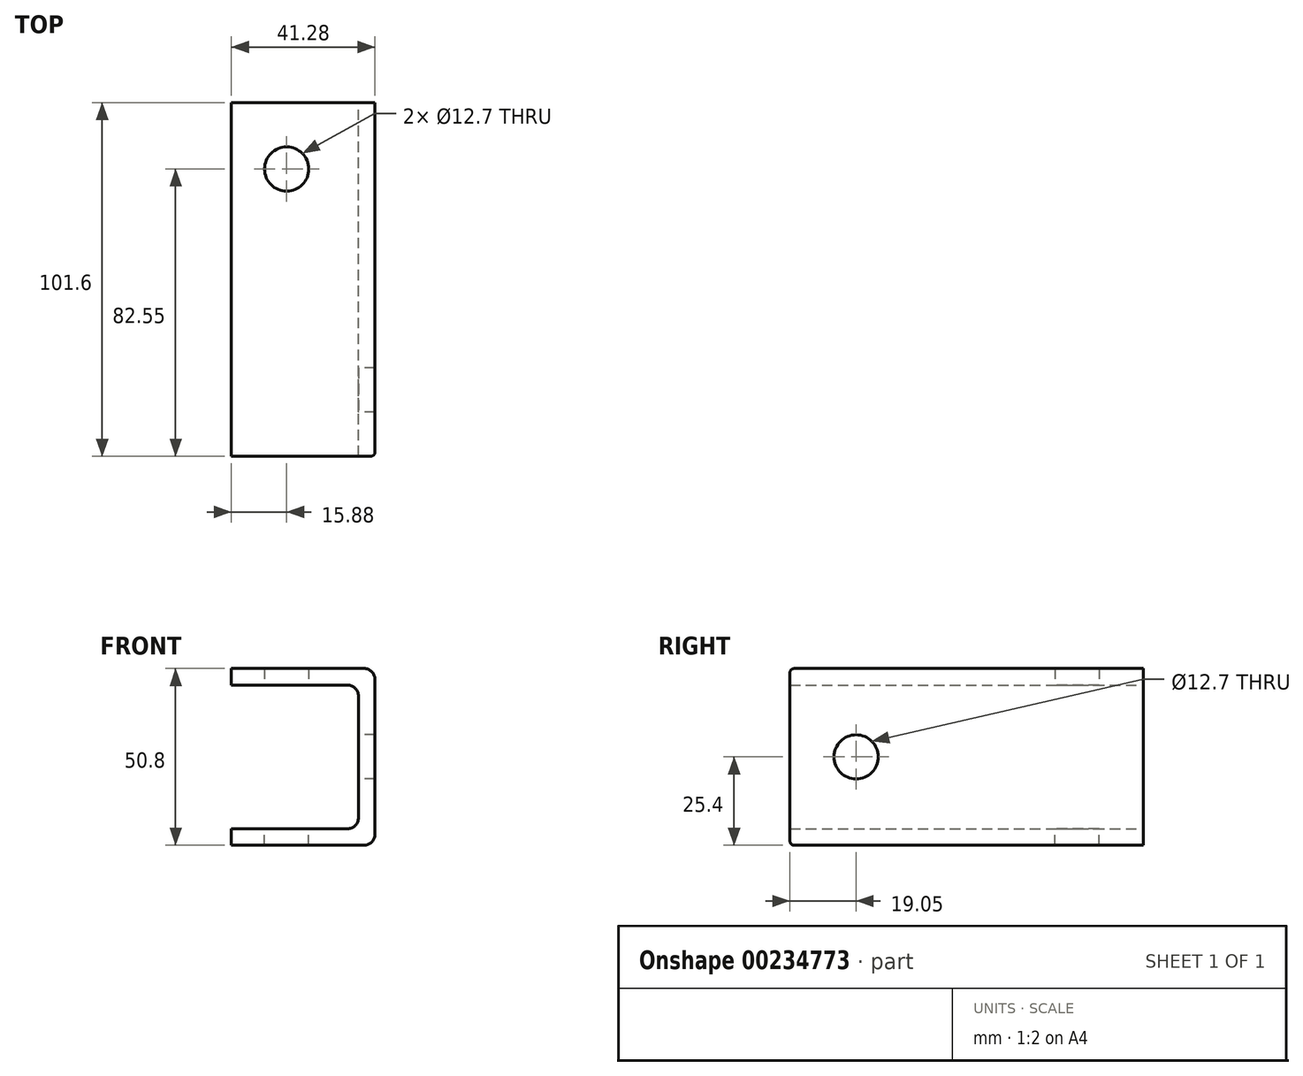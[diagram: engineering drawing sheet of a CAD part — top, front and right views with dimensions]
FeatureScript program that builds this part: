
annotation { "Feature Type Name" : "Feature", "Feature Type Description" : "" }
export const myFeature = defineFeature(function(context is Context, id is Id, definition is map)
    precondition{}
    {
        {
            var Q0;
            Q0=qCreatedBy(makeId("Front.planeOp"),FACE);
            var sketch = newSketch(context, id + "F0", { "sketchPlane" : qUnion([Q0])});
            skLineSegment(sketch, "E0.bottom", {"start": v(22.23, -25.4) * mm, "end": v(-22.23, -25.4) * mm});
            skLineSegment(sketch, "E0.top", {"start": v(22.23, 25.4) * mm, "end": v(-22.23, 25.4) * mm});
            skLineSegment(sketch, "E0.left", {"start": v(25.4, -22.23) * mm, "end": v(25.4, 22.23) * mm});
            skLineSegment(sketch, "E0.right", {"start": v(-25.4, -22.23) * mm, "end": v(-25.4, 22.23) * mm});
            skPoint(sketch, "E0.middle", {"position": v(0, 0) * mm});
            skLineSegment(sketch, "E1.bottom", {"start": v(17.46, -20.64) * mm, "end": v(-17.46, -20.64) * mm});
            skLineSegment(sketch, "E1.top", {"start": v(17.46, 20.64) * mm, "end": v(-17.46, 20.64) * mm});
            skLineSegment(sketch, "E1.left", {"start": v(20.64, -17.46) * mm, "end": v(20.64, 17.46) * mm});
            skLineSegment(sketch, "E1.right", {"start": v(-20.64, -17.46) * mm, "end": v(-20.64, 17.46) * mm});
            skPoint(sketch, "E2.visualSharp", {"position": v(-25.4, 25.4) * mm});
            skArc(sketch, "E2.filletArc", {"start": v(-22.23, 25.4) * mm, "mid": v(-24.47, 24.47) * mm, "end": v(-25.4, 22.23) * mm});
            skPoint(sketch, "E3.visualSharp", {"position": v(25.4, 25.4) * mm});
            skArc(sketch, "E3.filletArc", {"start": v(25.4, 22.23) * mm, "mid": v(24.47, 24.47) * mm, "end": v(22.23, 25.4) * mm});
            skPoint(sketch, "E4.visualSharp", {"position": v(20.64, 20.64) * mm});
            skArc(sketch, "E4.filletArc", {"start": v(20.64, 17.46) * mm, "mid": v(19.7, 19.7) * mm, "end": v(17.46, 20.64) * mm});
            skPoint(sketch, "E5.visualSharp", {"position": v(-20.64, 20.64) * mm});
            skArc(sketch, "E5.filletArc", {"start": v(-17.46, 20.64) * mm, "mid": v(-19.7, 19.7) * mm, "end": v(-20.64, 17.46) * mm});
            skPoint(sketch, "E6.visualSharp", {"position": v(-20.64, -20.64) * mm});
            skArc(sketch, "E6.filletArc", {"start": v(-20.64, -17.46) * mm, "mid": v(-19.7, -19.7) * mm, "end": v(-17.46, -20.64) * mm});
            skPoint(sketch, "E7.visualSharp", {"position": v(-25.4, -25.4) * mm});
            skArc(sketch, "E7.filletArc", {"start": v(-25.4, -22.23) * mm, "mid": v(-24.47, -24.47) * mm, "end": v(-22.23, -25.4) * mm});
            skPoint(sketch, "E8.visualSharp", {"position": v(20.64, -20.64) * mm});
            skArc(sketch, "E8.filletArc", {"start": v(17.46, -20.64) * mm, "mid": v(19.7, -19.7) * mm, "end": v(20.64, -17.46) * mm});
            skPoint(sketch, "E9.visualSharp", {"position": v(25.4, -25.4) * mm});
            skArc(sketch, "E9.filletArc", {"start": v(22.23, -25.4) * mm, "mid": v(24.47, -24.47) * mm, "end": v(25.4, -22.23) * mm});
            skSolve(sketch);
        }
        {
            var Q0;
            Q0=makeQuery(id+"F0.imprint","IMPRINT",FACE,{"disambiguationData":[TD([[makeQuery(id+"F0.imprint","IMPRINT",EDGE,{"derivedFrom":sQuery(id+"F0.wireOp",EDGE,"E0.bottom")}),-1.0]])]});
            extrude(context, id + "F7", {"entities" : qUnion([Q0]), "depth" : 101.6 * mm});
        }
        {
            var Q0;
            Q0=qCreatedBy(makeId("Top.planeOp"),FACE);
            var sketch = newSketch(context, id + "F1", { "sketchPlane" : qUnion([Q0])});
            skLineSegment(sketch, "E10.bottom", {"start": v(-15.88, 0) * mm, "end": v(-37.9, 0) * mm});
            skLineSegment(sketch, "E10.top", {"start": v(-20.64, -101.6) * mm, "end": v(-37.9, -101.6) * mm});
            skLineSegment(sketch, "E10.right", {"start": v(-37.9, 0) * mm, "end": v(-37.9, -101.6) * mm});
            skLineSegment(sketch, "E11", {"start": v(-15.88, -63.5) * mm, "end": v(25.4, -101.6) * mm});
            skLineSegment(sketch, "E12", {"start": v(25.4, -101.6) * mm, "end": v(-20.64, -101.6) * mm});
            skLineSegment(sketch, "E13", {"start": v(-15.88, -63.5) * mm, "end": v(-15.88, 0) * mm});
            skPoint(sketch, "E14", {"position": v(0, -19.05) * mm});
            skLineSegment(sketch, "E15", {"start": v(-15.88, -63.5) * mm, "end": v(-15.88, -101.6) * mm});
            skSolve(sketch);
        }
        {
            var Q0;
            Q0=makeQuery(id+"F1.imprint","IMPRINT",FACE,{"disambiguationData":[TD([[makeQuery(id+"F1.imprint","IMPRINT",EDGE,{"derivedFrom":sQuery(id+"F1.wireOp",EDGE,"E10.bottom")}),1.0]])]});
            extrude(context, id + "F2", {"entities" : qUnion([Q0]), "operationType" : NewBodyOperationType.REMOVE, "oppositeDirection" : true, "depth" : 25.4 * mm, "hasSecondDirection" : true, "secondDirectionOppositeDirection" : false, "secondDirectionDepth" : 25.4 * mm});
        }
        {
            var Q0;
            Q0=qCreatedBy(makeId("Right.planeOp"),FACE);
            var sketch = newSketch(context, id + "F3", { "sketchPlane" : qUnion([Q0])});
            skPoint(sketch, "E16", {"position": v(-82.55, 0) * mm});
            skPoint(sketch, "E17", {"position": v(0, 0) * mm});
            skSolve(sketch);
        }
        {
            var Q0;
            Q0=sQuery(id+"F3.wireOp",VERTEX,"E16");
            var Q1;
            Q1=sQuery(id+"F1.wireOp",VERTEX,"E14");
            var Q2;
            Q2=makeQuery(id+"F7.opExtrude","SWEPT_BODY",BODY,{"disambiguationData":[OSD([sQuery(id+"F0.wireOp",EDGE,"E0.bottom"),sQuery(id+"F0.wireOp",EDGE,"E0.top"),sQuery(id+"F0.wireOp",EDGE,"E0.left"),sQuery(id+"F0.wireOp",EDGE,"E0.right"),sQuery(id+"F0.wireOp",EDGE,"E1.bottom"),sQuery(id+"F0.wireOp",EDGE,"E1.top"),sQuery(id+"F0.wireOp",EDGE,"E1.left"),sQuery(id+"F0.wireOp",EDGE,"E1.right"),sQuery(id+"F0.wireOp",EDGE,"E2.filletArc"),sQuery(id+"F0.wireOp",EDGE,"E3.filletArc"),sQuery(id+"F0.wireOp",EDGE,"E4.filletArc"),sQuery(id+"F0.wireOp",EDGE,"E5.filletArc"),sQuery(id+"F0.wireOp",EDGE,"E6.filletArc"),sQuery(id+"F0.wireOp",EDGE,"E7.filletArc"),sQuery(id+"F0.wireOp",EDGE,"E8.filletArc"),sQuery(id+"F0.wireOp",EDGE,"E9.filletArc")])]});
            hole(context, id + "F4", {"style" : HoleStyle.SIMPLE, "endStyle" : HoleEndStyle.THROUGH, "oppositeDirection" : true, "holeDiameter" : 12.7 * mm, "locations" : qUnion([Q0, Q1]), "scope" : qUnion([Q2]), "isTappedThrough" : true});
        }
        {
            var Q0;
            Q0=sQuery(id+"F1.wireOp",VERTEX,"E14");
            var Q1;
            Q1=makeQuery(id+"F7.opExtrude","SWEPT_BODY",BODY,{"disambiguationData":[OSD([sQuery(id+"F0.wireOp",EDGE,"E0.bottom"),sQuery(id+"F0.wireOp",EDGE,"E0.top"),sQuery(id+"F0.wireOp",EDGE,"E0.left"),sQuery(id+"F0.wireOp",EDGE,"E0.right"),sQuery(id+"F0.wireOp",EDGE,"E1.bottom"),sQuery(id+"F0.wireOp",EDGE,"E1.top"),sQuery(id+"F0.wireOp",EDGE,"E1.left"),sQuery(id+"F0.wireOp",EDGE,"E1.right"),sQuery(id+"F0.wireOp",EDGE,"E2.filletArc"),sQuery(id+"F0.wireOp",EDGE,"E3.filletArc"),sQuery(id+"F0.wireOp",EDGE,"E4.filletArc"),sQuery(id+"F0.wireOp",EDGE,"E5.filletArc"),sQuery(id+"F0.wireOp",EDGE,"E6.filletArc"),sQuery(id+"F0.wireOp",EDGE,"E7.filletArc"),sQuery(id+"F0.wireOp",EDGE,"E8.filletArc"),sQuery(id+"F0.wireOp",EDGE,"E9.filletArc")])]});
            hole(context, id + "F5", {"style" : HoleStyle.SIMPLE, "endStyle" : HoleEndStyle.THROUGH, "holeDiameter" : 12.7 * mm, "locations" : qUnion([Q0]), "scope" : qUnion([Q1]), "isTappedThrough" : true});
        }
        {
            var Q0;
            Q0=makeQuery(id+"F2.boolean.opBoolean","MERGE",EDGE,{"derivedFrom":[makeQuery(id+"F7.opExtrude","CAP_EDGE",EDGE,{"disambiguationData":[OSD([sQuery(id+"F0.wireOp",EDGE,"E0.left")])],"isStart":false}),makeQuery(id+"F2.opExtrude","SWEPT_EDGE",EDGE,{"disambiguationData":[OSD([sQuery(id+"F1.wireOp",EDGE,"E11"),sQuery(id+"F1.wireOp",EDGE,"E12")])]})]});
            fillet(context, id + "F6", {"entities" : qUnion([Q0]), "radius" : 1.27 * mm, "tangentPropagation" : true, "allowEdgeOverflow" : false});
        }
    });
